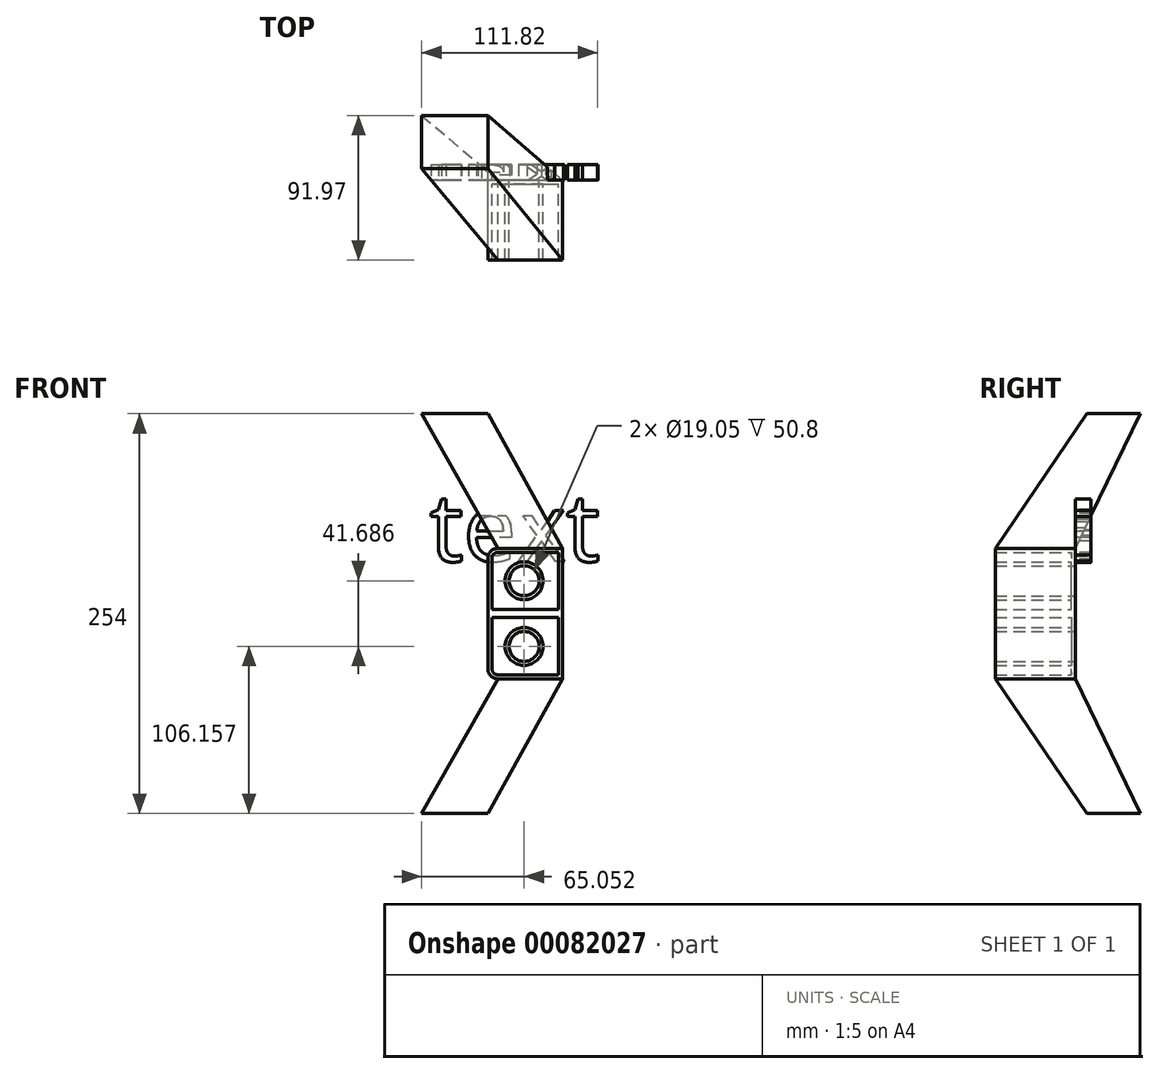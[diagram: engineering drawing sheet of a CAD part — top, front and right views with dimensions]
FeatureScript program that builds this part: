
annotation { "Feature Type Name" : "Feature", "Feature Type Description" : "" }
export const myFeature = defineFeature(function(context is Context, id is Id, definition is map)
    precondition{}
    {
        {
            var Q0;
            Q0=qCreatedBy(makeId("Front.planeOp"),FACE);
            var sketch = newSketch(context, id + "F0", { "sketchPlane" : qUnion([Q0])});
            skLineSegment(sketch, "E0.bottom", {"start": v(0, 0) * mm, "end": v(47.45, 0) * mm});
            skLineSegment(sketch, "E0.top", {"start": v(6.35, 41.4) * mm, "end": v(47.45, 41.4) * mm});
            skLineSegment(sketch, "E0.left", {"start": v(0, 0) * mm, "end": v(0, 35.05) * mm});
            skLineSegment(sketch, "E0.right", {"start": v(47.45, 0) * mm, "end": v(47.45, 41.4) * mm});
            skCircle(sketch, "E1", {"center": v(23.05, 20.84) * mm, "radius": 9.52 * mm});
            skPoint(sketch, "E2.visualSharp", {"position": v(0, 41.4) * mm});
            skArc(sketch, "E2.filletArc", {"start": v(6.35, 41.4) * mm, "mid": v(1.86, 39.54) * mm, "end": v(0, 35.05) * mm});
            skSolve(sketch);
        }
        {
            var Q0;
            Q0 = qSketchRegion(id + "F0", true);
            extrude(context, id + "F1", {"entities" : qUnion([Q0]), "depth" : 50.8 * mm});
        }
        {
            var Q0;
            Q0=qCreatedBy(makeId("Top.planeOp"),FACE);
            cPlane(context, id + "F2", {"entities" : qUnion([Q0]), "cplaneType" : CPlaneType.OFFSET, "offset" : 127 * mm, "width" : 152.4 * mm, "height" : 152.4 * mm});
        }
        {
            var Q0;
            Q0=qCreatedBy(id+"F2.planeOp",FACE);
            var sketch = newSketch(context, id + "F3", { "sketchPlane" : qUnion([Q0])});
            skLineSegment(sketch, "E3.bottom", {"start": v(0, 41.17) * mm, "end": v(-42, 41.17) * mm});
            skLineSegment(sketch, "E3.top", {"start": v(0, 7.28) * mm, "end": v(-42, 7.28) * mm});
            skLineSegment(sketch, "E3.left", {"start": v(0, 41.17) * mm, "end": v(0, 7.28) * mm});
            skLineSegment(sketch, "E3.right", {"start": v(-42, 41.17) * mm, "end": v(-42, 7.28) * mm});
            skSolve(sketch);
        }
        {
            var Q0;
            Q0=makeQuery(id+"F1.opExtrude","CAP_FACE",FACE,{"disambiguationData":[OSD([sQuery(id+"F0.wireOp",EDGE,"E0.bottom"),sQuery(id+"F0.wireOp",EDGE,"E0.top"),sQuery(id+"F0.wireOp",EDGE,"E0.left"),sQuery(id+"F0.wireOp",EDGE,"E0.right"),sQuery(id+"F0.wireOp",EDGE,"E1"),sQuery(id+"F0.wireOp",EDGE,"E2.filletArc")])],"isStart":false});
            shell(context, id + "F4", {"entities" : qUnion([Q0]), "thickness" : 2.54 * mm});
        }
        {
            var Q1;
            Q1=makeQuery(id+"F3.imprint","IMPRINT",FACE,{"disambiguationData":[TD([[makeQuery(id+"F3.imprint","IMPRINT",EDGE,{"derivedFrom":sQuery(id+"F3.wireOp",EDGE,"E3.bottom")}),1.0]])]});
            var Q2;
            Q2=makeQuery(id+"F1.opExtrude","SWEPT_FACE",FACE,{"disambiguationData":[OSD([sQuery(id+"F0.wireOp",EDGE,"E0.top")])]});
            loft(context, id + "F5", {"operationType" : NewBodyOperationType.ADD, "sheetProfilesArray" : [{ "sheetProfileEntities" : qUnion([Q1]) }, { "sheetProfileEntities" : qUnion([Q2]) }]});
        }
        {
            var Q0;
            Q0=makeQuery(id+"F1.opExtrude","SWEPT_BODY",BODY,{"disambiguationData":[OSD([sQuery(id+"F0.wireOp",EDGE,"E0.bottom"),sQuery(id+"F0.wireOp",EDGE,"E0.top"),sQuery(id+"F0.wireOp",EDGE,"E0.left"),sQuery(id+"F0.wireOp",EDGE,"E0.right"),sQuery(id+"F0.wireOp",EDGE,"E1"),sQuery(id+"F0.wireOp",EDGE,"E2.filletArc")])]});
            var Q1;
            Q1=qCreatedBy(makeId("Top.planeOp"),FACE);
            mirror(context, id + "F6", {"operationType" : NewBodyOperationType.ADD, "entities" : qUnion([Q0]), "mirrorPlane" : qUnion([Q1])});
        }
        {
            var Q0;
            Q0=qCreatedBy(makeId("Front.planeOp"),FACE);
            var sketch = newSketch(context, id + "F7", { "sketchPlane" : qUnion([Q0])});
            skText(sketch, "E4", { "text": "text", "fontName": "OpenSans-Regular.ttf"});
            const initialGuessF7  = {"E4": [-0.03687, 0.03313, 1, 0, 0.0434]};
            skSetInitialGuess(sketch, initialGuessF7);
            skSolve(sketch);
        }
        {
            var Q0;
            Q0 = qSketchRegion(id + "F7", true);
            extrude(context, id + "F8", {"entities" : qUnion([Q0]), "operationType" : NewBodyOperationType.ADD, "oppositeDirection" : true, "depth" : 10 * mm});
        }
    });
